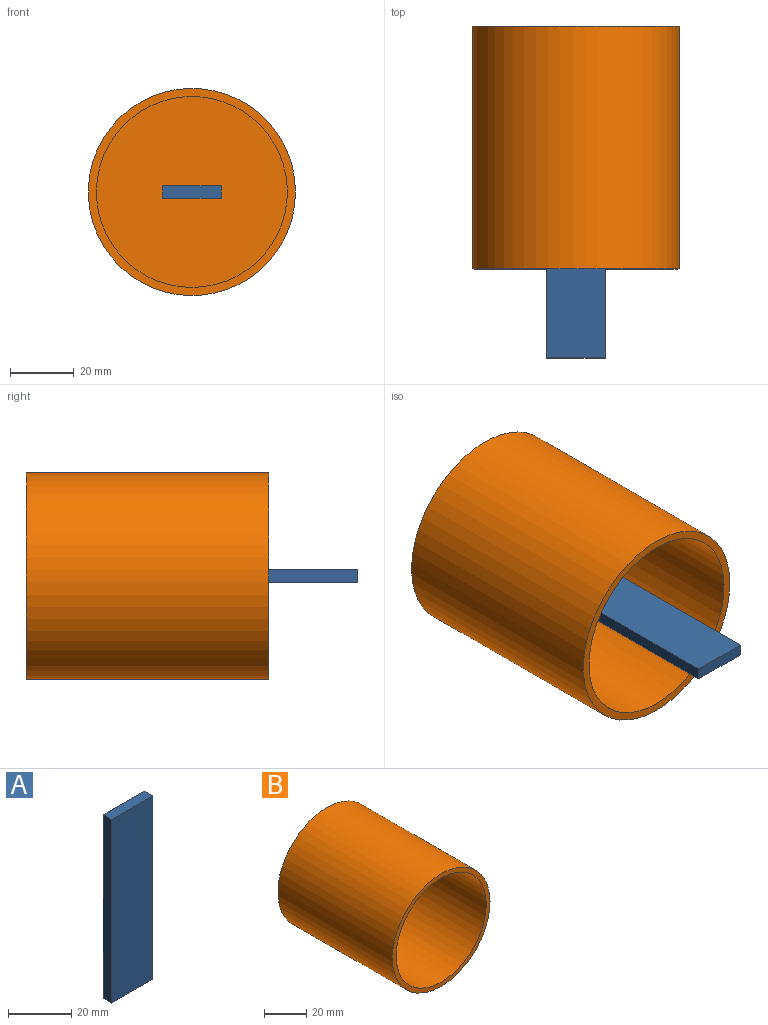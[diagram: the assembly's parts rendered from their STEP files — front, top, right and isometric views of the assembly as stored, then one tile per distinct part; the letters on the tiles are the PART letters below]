
ASSEMBLY  parts=2 mates=1
PART A: 6 faces, bbox 18.4x3.8x71 mm
  f0: plane 18.4x3.81mm, normal (0,0,1), area 70.1mm2, adj f1,f3,f4,f5
  f1: plane 71.03x3.81mm, normal (-1,0,0), area 270.6mm2, adj f0,f2,f4,f5
  f2: plane 18.4x3.81mm, normal (0,0,-1), area 70.1mm2, adj f1,f3,f4,f5
  f3: plane 71.03x3.81mm, normal (1,0,0), area 270.6mm2, adj f0,f2,f4,f5
  f4: plane 71.03x18.4mm, normal (0,-1,0), area 1307.2mm2, adj f0,f1,f2,f3
  f5: plane 71.03x18.4mm, normal (0,1,0), area 1307.2mm2, adj f0,f1,f2,f3
PART B: 5 faces, bbox 65x76.2x65 mm
  f0: cylinder r=32.5mm len=76.2mm, axis (0,1,0), area 15560.3mm2, adj f1,f2
  f1: plane 65x65mm, normal (0,-1,0), area 498.4mm2, adj f0,f3
  f2: plane 65x65mm, normal (0,1,0), area 3318.3mm2, adj f0
  f3: cylinder r=29.96mm len=73.66mm, axis (0,1,0), area 13866.1mm2, adj f1,f4
  f4: plane 59.92x59.92mm, normal (0,-1,0), area 2819.9mm2, adj f3
PLACE A rot(axis=(-1,0,0),90deg) t=(-56.63,-97.75,60.94)mm
PLACE B t=(-56.63,-29.13,62.85)mm
MATE fastened A.f2 <-> B.f0  axis (0,-1,0) through (-56.63,-133.27,62.85)mm
